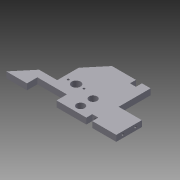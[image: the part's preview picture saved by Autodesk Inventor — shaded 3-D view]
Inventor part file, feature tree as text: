
AUTODESK INVENTOR PART (.ipt)
format: ipt  version: 2012 (Build 160160000, 160)  size: 235,520 bytes
history: native  units: mm
features: sketch x17, reference x16, extrude x9, hole x8, projected_geometry x1
ambient origin geometry x8: Origin, YZ Plane, XZ Plane, XY Plane, X Axis, Y Axis, Z Axis, Center Point
bodies: Solid1 (feature_tree)
feature tree (51):
  extrude  "Extrusion1"  Depth=91.44mm
  sketch  "Sketch11"  dims[d119=9.525mm d120=0.0mm d121=12.7mm]
  sketch  "Sketch8"  dims[d3=9.525mm d4=0.0mm d101=8.726646mm]
  sketch  "Sketch9"  dims[d105=14.0mm d106=9.525mm d107=0.0mm]
  extrude  "Extrusion2"  Depth=8.726646mm
  hole  "Hole7"  [1 undecoded]
  extrude  "Extrusion3"  Depth=12.7mm
  extrude  "Extrusion4"  Depth=12.7mm
  extrude  "Extrusion5"  Depth=9.525mm TaperAngle=0.0deg
  extrude  "Extrusion6"  Depth=16.51mm TaperAngle=0.0deg
  extrude  "Extrusion7"  Depth=50.8mm TaperAngle=0.0deg
  extrude  "Extrusion8"  Depth=101.6mm
  extrude  "Extrusion9"  Depth=9.525mm
  hole  "Hole8"  [1 undecoded]
  hole  "Hole9"  [1 undecoded]
  hole  "Hole10"  [1 undecoded]
  hole  "Hole11"  [1 undecoded]
  hole  "Hole12"  [1 undecoded]
  hole  "Hole13"  [1 undecoded]
  hole  "Hole14"  [1 undecoded]
  sketch  "Sketch1"  dims[d0=175.0mm d1=91.44mm]
  reference  "Reference6"
  reference  "Reference9"
  reference  "Reference10"
  sketch  "Sketch10"  dims[d108=3.4036mm d109=9.525mm d110=4.0mm d111=2.0mm d112=90.0deg d113=8.0mm d114=20.594885mm d118=12.7mm]
  reference  "Reference14"
  reference  "Reference15"
  reference  "Reference16"
  sketch  "Sketch12"  dims[d122=13.8938mm d123=9.525mm d124=0.0mm]
  sketch  "Sketch13"  dims[d126=46.99mm d127=16.51mm d128=0.0mm]
  sketch  "Sketch14"  dims[d129=36.83mm d130=50.8mm d131=0.0mm]
  projected_geometry  "Projected Loop1"
  sketch  "Sketch15"  dims[d132=24.13mm d133=101.6mm]
  sketch  "Sketch16"  dims[d134=62.992mm d135=0.0mm d136=9.525mm]
  sketch  "Sketch17"  dims[d137=38.1mm d138=9.525mm d139=0.0mm]
  reference  "Reference19"
  sketch  "Sketch18"  dims[d140=38.1mm d141=9.525mm]
  reference  "Reference20"
  sketch  "Sketch19"  dims[d142=9.525mm d143=0.0mm]
  reference  "Reference21"
  reference  "Reference22"
  sketch  "Sketch20"  dims[d144=3.302mm d145=12.7mm d146=9.525mm d147=6.35mm d148=14.3117mm d149=12.7mm d150=20.594885mm]
  sketch  "Sketch21"  dims[d151=3.302mm d152=12.7mm d153=9.525mm d154=6.35mm d155=14.3117mm d156=12.7mm d157=20.594885mm]
  reference  "Reference23"
  reference  "Reference24"
  sketch  "Sketch22"  dims[d158=3.302mm d159=12.7mm d160=9.525mm d161=6.35mm d162=14.3117mm d163=12.7mm d164=20.594885mm d165=30.48mm]
  reference  "Reference25"
  reference  "Reference26"
  reference  "Reference27"
  sketch  "Sketch23"  dims[d166=10.16mm d167=10.16mm d168=3.302mm d169=12.7mm d170=9.525mm d171=6.35mm d172=14.3117mm d173=12.7mm d174=20.594885mm d175=2.159mm d176=12.7mm d177=9.525mm d178=6.35mm d179=14.3117mm d180=5.08mm d181=20.594885mm d182=3.302mm d183=12.7mm d184=9.525mm d185=6.35mm d186=14.3117mm d187=5.08mm d188=20.594885mm d189=3.302mm d190=12.7mm d191=9.525mm d192=6.35mm d193=14.3117mm d194=7.62mm d195=20.594885mm d196=94.99mm d63=1.0mm d64=1.0mm]
  reference  "Reference28"
note: 8 required parameter values undecoded (feature->parameter linkage not recoverable at this tier; creation-order binding heuristic only, values carry confidence <= 0.55)
